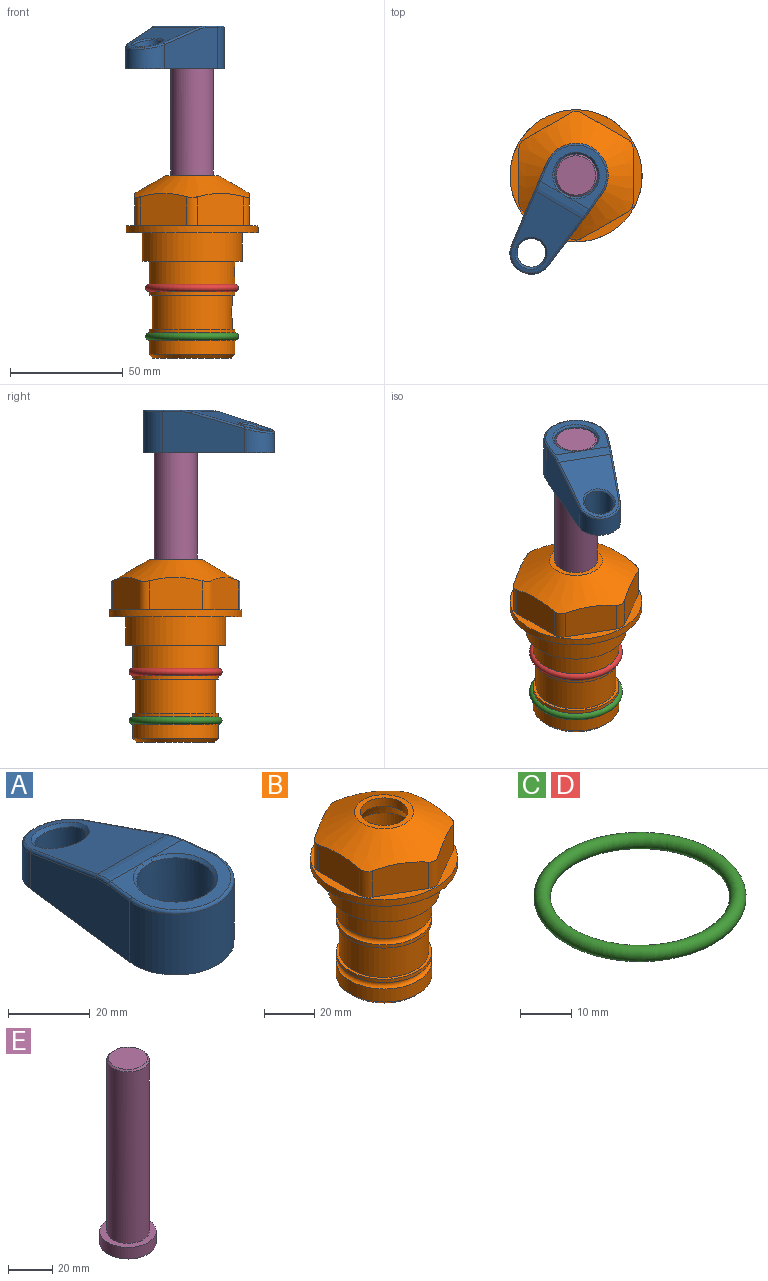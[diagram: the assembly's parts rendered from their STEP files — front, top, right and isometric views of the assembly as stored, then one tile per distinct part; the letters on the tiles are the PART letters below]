
ASSEMBLY  parts=5 mates=4
PART A: 31 faces, bbox 31.7x65.5x19.8 mm
  f0: plane 39.12x18.26mm, normal (0.99,0.12,0), area 612.2mm2, adj f1,f4,f7,f11,f13,f15
  f1: cylinder r=9.53mm len=18.91mm, axis (0,0,-1), area 296.1mm2, adj f0,f2,f7,f17
  f2: plane 39.12x18.26mm, normal (-0.99,0.12,0), area 612.2mm2, adj f1,f4,f7,f12,f14,f16
  f3: cylinder r=6.35mm len=12.7mm, axis (0,0,-1), area 362.4mm2, adj f7,f18
  f4: cylinder r=14.29mm len=28.58mm, axis (0,0,-1), area 882.2mm2, adj f0,f2,f7,f10
  f5: cylinder r=9.53mm len=19.05mm, axis (0,0,-1), area 1092.6mm2, adj f7,f19,f20
  f6: plane 26.99x23.69mm, normal (0,0,1), area 216.2mm2, adj f9,f10,f11,f12,f19
  f7: plane 63.5x28.58mm, normal (0,0,-1), area 661.8mm2, adj f0,f1,f2,f3,f4,f5,f22,f23
  f8: plane 33.52x23.6mm, normal (0,0.26,0.97), area 486mm2, adj f9,f15,f16,f17,f18
  f9: cylinder r=19.05mm len=24.72mm, axis (1,0,0), area 120.4mm2, adj f6,f8,f13,f14,f20
  f10: torus R=13.49mm, axis (0,0,1), area 59mm2, adj f4,f6,f11,f12
  f11: cylinder r=0.79mm len=8.67mm, axis (0.12,-0.99,0), area 10.8mm2, adj f0,f6,f10,f13
  f12: cylinder r=0.79mm len=8.67mm, axis (0.12,0.99,0), area 10.8mm2, adj f2,f6,f10,f14
  f13: bspline ~4.95x1.42mm, area 6.1mm2, adj f0,f9,f11,f15
  f14: bspline ~4.95x1.42mm, area 6.1mm2, adj f2,f9,f12,f16
  f15: cylinder r=0.79mm len=25.95mm, axis (0.12,-0.96,0.26), area 32.9mm2, adj f0,f8,f13,f17
  f16: cylinder r=0.79mm len=25.95mm, axis (0.12,0.96,-0.26), area 32.9mm2, adj f2,f8,f14,f17
  f17: bspline ~18.91x8.38mm, area 30mm2, adj f1,f8,f15,f16
  f18: bspline ~14.29x14.29mm, area 48.3mm2, adj f3,f8
  f19: cone r=9.53mm half-angle=45deg, axis (0,0,1), area 66.5mm2, adj f5,f6,f20
  f20: bspline ~3.22x0.96mm, area 3.5mm2, adj f5,f9,f19
  f21: plane 2.75x2.72mm, normal (0,0,-1), area 2.9mm2, adj f23,f25,f28
  f22: plane 23.05x15.88mm, normal (-0.99,-0.12,0), area 323.6mm2, adj f7,f25,f26,f27,f28,f29
  f23: plane 23.05x15.88mm, normal (0.99,-0.12,0), area 323.6mm2, adj f7,f21,f25,f27,f28,f30
  f24: cylinder r=9.53mm len=10.69mm, axis (0,0,-1), area 114.7mm2, adj f7,f27,f29,f30
  f25: cylinder r=12.7mm len=20.59mm, axis (0,0,-1), area 381.1mm2, adj f7,f21,f22,f23,f26,f28
  f26: plane 2.75x2.72mm, normal (0,0,-1), area 2.9mm2, adj f22,f25,f28
  f27: plane 19.72x18.37mm, normal (0,-0.26,-0.97), area 291.8mm2, adj f22,f23,f24,f28,f29,f30
  f28: cylinder r=15.88mm len=19.92mm, axis (1,0,0), area 54.8mm2, adj f21,f22,f23,f25,f26,f27
  f29: cylinder r=1.59mm len=11mm, axis (0,0,-1), area 34.7mm2, adj f7,f22,f24,f27
  f30: cylinder r=1.59mm len=11mm, axis (0,0,-1), area 34.7mm2, adj f7,f23,f24,f27
PART B: 36 faces, bbox 58.7x58.7x81 mm
  f0: cylinder r=17.78mm len=35.56mm, axis (0,0,1), area 1670.8mm2, adj f23,f24,f31
  f1: cylinder r=19.05mm len=38.1mm, axis (0,0,1), area 1191.9mm2, adj f26,f27,f30
  f2: plane 58.66x58.66mm, normal (0,0,-1), area 1150.6mm2, adj f3,f28
  f3: cylinder r=29.33mm len=58.66mm, axis (0,0,-1), area 585.1mm2, adj f2,f4
  f4: plane 58.66x58.66mm, normal (0,0,1), area 475.9mm2, adj f3,f5,f6,f7,f8,f9,f10,f11
  f5: plane 20.32x14.34mm, normal (-0.5,0.87,0), area 324.4mm2, adj f4,f15,f16,f17
  f6: plane 20.32x14.34mm, normal (0.5,0.87,0), area 324.4mm2, adj f4,f14,f15,f17
  f7: plane 23.48x14.34mm, normal (1,0,0), area 324.4mm2, adj f4,f13,f14,f17
  f8: plane 20.32x14.34mm, normal (0.5,-0.87,0), area 324.4mm2, adj f4,f12,f13,f17
  f9: plane 20.32x14.34mm, normal (-0.5,-0.87,0), area 324.4mm2, adj f4,f11,f12,f17
  f10: plane 23.48x14.34mm, normal (-1,0,0), area 324.4mm2, adj f4,f11,f16,f17
  f11: cylinder r=5.08mm len=12.85mm, axis (0,0,-1), area 67.2mm2, adj f4,f9,f10,f17
  f12: cylinder r=5.08mm len=12.85mm, axis (0,0,-1), area 67.2mm2, adj f4,f8,f9,f17
  f13: cylinder r=5.08mm len=12.85mm, axis (0,0,-1), area 67.2mm2, adj f4,f7,f8,f17
  f14: cylinder r=5.08mm len=12.85mm, axis (0,0,-1), area 67.2mm2, adj f4,f6,f7,f17
  f15: cylinder r=5.08mm len=12.85mm, axis (0,0,-1), area 67.2mm2, adj f4,f5,f6,f17
  f16: cylinder r=5.08mm len=12.85mm, axis (0,0,-1), area 67.2mm2, adj f4,f5,f10,f17
  f17: cone r=11.73mm half-angle=60deg, axis (0,0,-1), area 2071.8mm2, adj f5,f6,f7,f8,f9,f10,f11,f12
  f18: plane 23.46x23.46mm, normal (0,0,1), area 147.4mm2, adj f17,f35
  f19: plane 34.93x34.93mm, normal (0,0,-1), area 958mm2, adj f29
  f20: cylinder r=19.05mm len=38.1mm, axis (0,0,1), area 760.1mm2, adj f21,f29
  f21: torus R=19.05mm, axis (0,0,1), area 565.3mm2, adj f20,f22
  f22: cylinder r=19.05mm len=38.1mm, axis (0,0,1), area 190mm2, adj f21,f23
  f23: plane 38.1x38.1mm, normal (0,0,1), area 146.9mm2, adj f0,f22
  f24: plane 38.1x38.1mm, normal (0,0,-1), area 146.9mm2, adj f0,f25
  f25: cylinder r=19.05mm len=38.1mm, axis (0,0,1), area 190mm2, adj f24,f26
  f26: torus R=19.05mm, axis (0,0,1), area 565.3mm2, adj f1,f25
  f27: plane 44.45x44.45mm, normal (0,0,-1), area 411.7mm2, adj f1,f28
  f28: cylinder r=22.23mm len=44.45mm, axis (0,0,1), area 1773.5mm2, adj f2,f27
  f29: cone r=19.05mm half-angle=45deg, axis (0,0,1), area 257.5mm2, adj f19,f20
  f30: cylinder r=3.17mm len=6.75mm, axis (-1,0,0), area 128mm2, adj f1,f33
  f31: cylinder r=3.17mm len=6.35mm, axis (-1,0,0), area 102.5mm2, adj f0,f33
  f32: plane 25.4x25.4mm, normal (0,0,1), area 506.7mm2, adj f33
  f33: cylinder r=12.7mm len=66.42mm, axis (0,0,-1), area 5236.2mm2, adj f30,f31,f32,f34
  f34: cone r=9.53mm half-angle=30deg, axis (0,0,-1), area 443.4mm2, adj f33,f35
  f35: cylinder r=9.53mm len=19.05mm, axis (0,0,-1), area 240.9mm2, adj f18,f34
PART C: 1 faces, bbox 44.7x44.7x3.2 mm
  f0: torus R=19.05mm, axis (0,0,1), area 1193.9mm2
PART D: same geometry as C
PART E: 6 faces, bbox 25.4x25.4x101.6 mm
  f0: plane 17.46x17.46mm, normal (0,0,1), area 239.5mm2, adj f5
  f1: plane 25.4x25.4mm, normal (0,0,-1), area 506.7mm2, adj f2
  f2: cylinder r=12.7mm len=25.4mm, axis (0,0,1), area 506.7mm2, adj f1,f3
  f3: plane 25.4x25.4mm, normal (0,0,1), area 221.7mm2, adj f2,f4
  f4: cylinder r=9.53mm len=94.46mm, axis (0,0,1), area 5653mm2, adj f3,f5
  f5: cone r=8.73mm half-angle=45deg, axis (0,0,-1), area 64.4mm2, adj f0,f4
PLACE A rot(axis=(0,0,1),150deg) t=(0,0,28.35)mm
PLACE B at identity fixed
PLACE C t=(0,0,-21.59)mm
PLACE D at identity
PLACE E rot(axis=(0,0,1),150deg) t=(0,0,27.55)mm
MATE fastened C.f0 <-> B.f0  axis (0,0,1) through (0,0,-46.1)mm
MATE fastened D.f0 <-> B.f0  axis (0,0,1) through (0,0,-24.51)mm
MATE fastened A.f4 <-> E.f2  axis (0,0,1) through (0,0,91.05)mm
MATE cylindrical B.f0 <-> E.f2  axis (0,0,1) through (0,0,-50.55)mm
